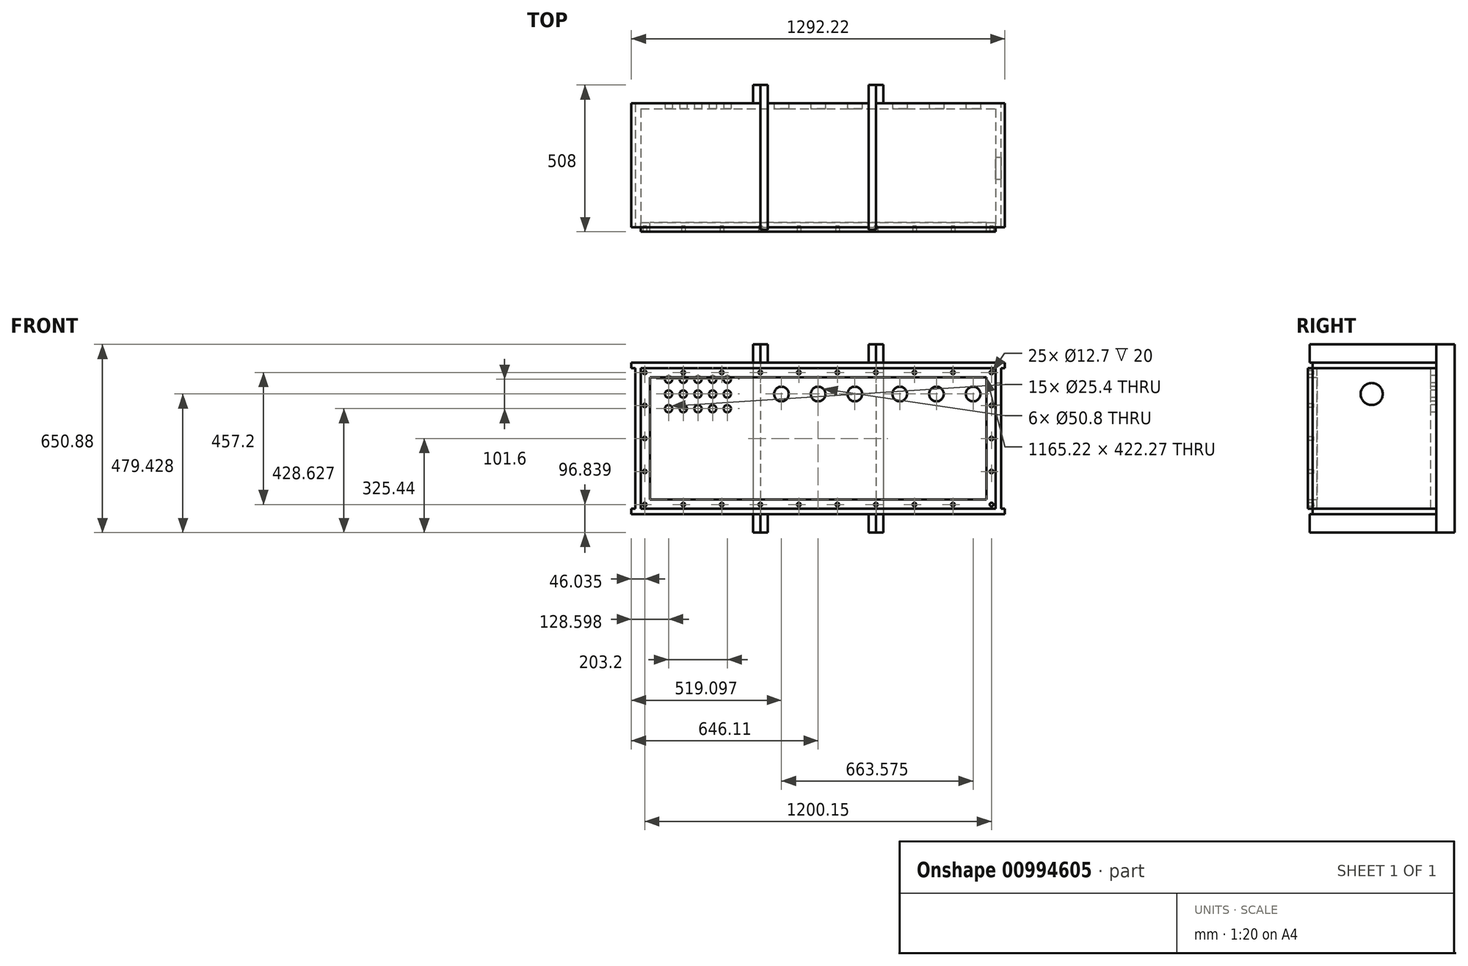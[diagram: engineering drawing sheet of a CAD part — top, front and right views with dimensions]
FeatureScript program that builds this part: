
annotation { "Feature Type Name" : "Feature", "Feature Type Description" : "" }
export const myFeature = defineFeature(function(context is Context, id is Id, definition is map)
    precondition{}
    {
        {
            var Q0;
            Q0=qCreatedBy(makeId("Front.planeOp"),FACE);
            var sketch = newSketch(context, id + "F0", { "sketchPlane" : qUnion([Q0])});
            skLineSegment(sketch, "E0.bottom", {"start": v(-633.41, -261.94) * mm, "end": v(633.41, -261.94) * mm});
            skLineSegment(sketch, "E0.top", {"start": v(-633.41, 261.94) * mm, "end": v(633.41, 261.94) * mm});
            skLineSegment(sketch, "E0.left", {"start": v(-633.41, -261.94) * mm, "end": v(-633.41, 261.94) * mm});
            skLineSegment(sketch, "E0.right", {"start": v(633.41, -261.94) * mm, "end": v(633.41, 261.94) * mm});
            skPoint(sketch, "E0.middle", {"position": v(0, 0) * mm});
            skSolve(sketch);
        }
        {
            var Q0;
            Q0=makeQuery(id+"F0.imprint","IMPRINT",FACE,{"disambiguationData":[TD([[makeQuery(id+"F0.imprint","IMPRINT",EDGE,{"derivedFrom":sQuery(id+"F0.wireOp",EDGE,"E0.bottom")}),1.0]])]});
            extrude(context, id + "F1", {"entities" : qUnion([Q0]), "depth" : 428.62 * mm, "offsetDistance" : 25 * mm});
        }
        {
            var Q0;
            Q0=makeQuery(id+"F1.opExtrude","CAP_FACE",FACE,{"disambiguationData":[OSD([sQuery(id+"F0.wireOp",EDGE,"E0.bottom"),sQuery(id+"F0.wireOp",EDGE,"E0.top"),sQuery(id+"F0.wireOp",EDGE,"E0.left"),sQuery(id+"F0.wireOp",EDGE,"E0.right")])],"isStart":false});
            var sketch = newSketch(context, id + "F2", { "sketchPlane" : qUnion([Q0])});
            skLineSegment(sketch, "E1.bottom", {"start": v(-614.36, -242.89) * mm, "end": v(614.36, -242.89) * mm});
            skLineSegment(sketch, "E1.top", {"start": v(-614.36, 242.89) * mm, "end": v(614.36, 242.89) * mm});
            skLineSegment(sketch, "E1.left", {"start": v(-614.36, -242.89) * mm, "end": v(-614.36, 242.89) * mm});
            skLineSegment(sketch, "E1.right", {"start": v(614.36, -242.89) * mm, "end": v(614.36, 242.89) * mm});
            skPoint(sketch, "E1.middle", {"position": v(0, 0) * mm});
            skSolve(sketch);
        }
        {
            var Q0;
            Q0=makeQuery(id+"F2.imprint","IMPRINT",FACE,{"disambiguationData":[TD([[makeQuery(id+"F2.imprint","IMPRINT",EDGE,{"derivedFrom":sQuery(id+"F2.wireOp",EDGE,"E1.bottom")}),1.0]])]});
            extrude(context, id + "F3", {"entities" : qUnion([Q0]), "operationType" : NewBodyOperationType.REMOVE, "oppositeDirection" : true, "depth" : 409.57 * mm, "offsetDistance" : 25 * mm});
        }
        {
            var Q0;
            Q0=makeQuery(id+"F1.opExtrude","CAP_FACE",FACE,{"disambiguationData":[OSD([sQuery(id+"F0.wireOp",EDGE,"E0.bottom"),sQuery(id+"F0.wireOp",EDGE,"E0.top"),sQuery(id+"F0.wireOp",EDGE,"E0.left"),sQuery(id+"F0.wireOp",EDGE,"E0.right")])],"isStart":false});
            var sketch = newSketch(context, id + "F4", { "sketchPlane" : qUnion([Q0])});
            skLineSegment(sketch, "E2.bottom", {"start": v(614.36, 242.89) * mm, "end": v(-614.36, 242.89) * mm});
            skLineSegment(sketch, "E2.top", {"start": v(614.36, -242.89) * mm, "end": v(-614.36, -242.89) * mm});
            skLineSegment(sketch, "E2.left", {"start": v(614.36, 242.89) * mm, "end": v(614.36, -242.89) * mm});
            skLineSegment(sketch, "E2.right", {"start": v(-614.36, 242.89) * mm, "end": v(-614.36, -242.89) * mm});
            skPoint(sketch, "E2.middle", {"position": v(0, 0) * mm});
            skLineSegment(sketch, "E3.bottom", {"start": v(582.61, 211.14) * mm, "end": v(-582.61, 211.14) * mm});
            skLineSegment(sketch, "E3.top", {"start": v(582.61, -211.14) * mm, "end": v(-582.61, -211.14) * mm});
            skLineSegment(sketch, "E3.left", {"start": v(582.61, 211.14) * mm, "end": v(582.61, -211.14) * mm});
            skLineSegment(sketch, "E3.right", {"start": v(-582.61, 211.14) * mm, "end": v(-582.61, -211.14) * mm});
            skSolve(sketch);
        }
        {
            var Q0;
            Q0 = qSketchRegion(id + "F4", true);
            extrude(context, id + "F5", {"entities" : qUnion([Q0]), "endBound" : BoundingType.SYMMETRIC, "depth" : 31.75 * mm, "offsetDistance" : 25 * mm});
        }
        {
            var Q0;
            Q0=makeQuery(id+"F5.opExtrude","CAP_FACE",FACE,{"disambiguationData":[OSD([sQuery(id+"F4.wireOp",EDGE,"E2.bottom"),sQuery(id+"F4.wireOp",EDGE,"E2.top"),sQuery(id+"F4.wireOp",EDGE,"E2.left"),sQuery(id+"F4.wireOp",EDGE,"E2.right"),sQuery(id+"F4.wireOp",EDGE,"E3.bottom"),sQuery(id+"F4.wireOp",EDGE,"E3.top"),sQuery(id+"F4.wireOp",EDGE,"E3.left"),sQuery(id+"F4.wireOp",EDGE,"E3.right")])],"isStart":false});
            var sketch = newSketch(context, id + "F6", { "sketchPlane" : qUnion([Q0])});
            skLineSegment(sketch, "E4", {"start": v(-600.08, 242.89) * mm, "end": v(-600.07, -242.89) * mm, "construction": true});
            skLineSegment(sketch, "E5", {"start": v(-614.36, 228.6) * mm, "end": v(614.36, 228.6) * mm, "construction": true});
            skLineSegment(sketch, "E6", {"start": v(-614.36, -228.6) * mm, "end": v(614.36, -228.6) * mm, "construction": true});
            skLineSegment(sketch, "E7", {"start": v(600.07, 242.89) * mm, "end": v(600.07, -242.89) * mm, "construction": true});
            skPoint(sketch, "E8", {"position": v(-600.08, 228.6) * mm});
            skCircle(sketch, "E9", {"center": v(-600.08, 228.6) * mm, "radius": 6.35 * mm});
            skCircle(sketch, "E10.1.0.0", {"center": v(-466.73, 228.6) * mm, "radius": 6.35 * mm});
            skCircle(sketch, "E10.2.0.0", {"center": v(-333.38, 228.6) * mm, "radius": 6.35 * mm});
            skCircle(sketch, "E10.3.0.0", {"center": v(-200.03, 228.6) * mm, "radius": 6.35 * mm});
            skCircle(sketch, "E10.4.0.0", {"center": v(-66.68, 228.6) * mm, "radius": 6.35 * mm});
            skCircle(sketch, "E10.5.0.0", {"center": v(66.67, 228.6) * mm, "radius": 6.35 * mm});
            skCircle(sketch, "E10.6.0.0", {"center": v(200.02, 228.6) * mm, "radius": 6.35 * mm});
            skCircle(sketch, "E10.7.0.0", {"center": v(333.37, 228.6) * mm, "radius": 6.35 * mm});
            skCircle(sketch, "E10.8.0.0", {"center": v(466.72, 228.6) * mm, "radius": 6.35 * mm});
            skCircle(sketch, "E10.9.0.0", {"center": v(600.07, 228.6) * mm, "radius": 6.35 * mm});
            skLineSegment(sketch, "E10.direction1", {"start": v(-600.08, 228.6) * mm, "end": v(-466.73, 228.6) * mm, "construction": true});
            skCircle(sketch, "E11.0.1.0", {"center": v(-600.08, 114.3) * mm, "radius": 6.35 * mm});
            skCircle(sketch, "E11.0.2.0", {"center": v(-600.08, 0) * mm, "radius": 6.35 * mm});
            skCircle(sketch, "E11.0.3.0", {"center": v(-600.08, -114.3) * mm, "radius": 6.35 * mm});
            skCircle(sketch, "E11.0.4.0", {"center": v(-600.08, -228.6) * mm, "radius": 6.35 * mm});
            skLineSegment(sketch, "E11.direction1", {"start": v(-600.08, 228.6) * mm, "end": v(-590.78, 228.6) * mm, "construction": true});
            skLineSegment(sketch, "E11.direction2", {"start": v(-600.08, 228.6) * mm, "end": v(-600.08, 114.3) * mm, "construction": true});
            skCircle(sketch, "E12.1.0.0", {"center": v(-466.73, -228.6) * mm, "radius": 6.35 * mm});
            skCircle(sketch, "E12.2.0.0", {"center": v(-333.38, -228.6) * mm, "radius": 6.35 * mm});
            skCircle(sketch, "E12.3.0.0", {"center": v(-200.03, -228.6) * mm, "radius": 6.35 * mm});
            skCircle(sketch, "E12.4.0.0", {"center": v(-66.68, -228.6) * mm, "radius": 6.35 * mm});
            skCircle(sketch, "E12.5.0.0", {"center": v(66.67, -228.6) * mm, "radius": 6.35 * mm});
            skCircle(sketch, "E12.6.0.0", {"center": v(200.02, -228.6) * mm, "radius": 6.35 * mm});
            skCircle(sketch, "E12.7.0.0", {"center": v(333.37, -228.6) * mm, "radius": 6.35 * mm});
            skCircle(sketch, "E12.8.0.0", {"center": v(466.72, -228.6) * mm, "radius": 6.35 * mm});
            skCircle(sketch, "E12.9.0.0", {"center": v(600.07, -228.6) * mm, "radius": 6.35 * mm});
            skLineSegment(sketch, "E12.direction1", {"start": v(-600.08, -228.6) * mm, "end": v(-466.73, -228.6) * mm, "construction": true});
            skCircle(sketch, "E13.0.1.0", {"center": v(600.07, 114.29) * mm, "radius": 6.35 * mm});
            skCircle(sketch, "E13.0.2.0", {"center": v(600.07, -0.02) * mm, "radius": 6.35 * mm});
            skCircle(sketch, "E13.0.3.0", {"center": v(600.07, -114.33) * mm, "radius": 6.35 * mm});
            skCircle(sketch, "E13.0.4.0", {"center": v(600.07, -228.64) * mm, "radius": 6.35 * mm});
            skLineSegment(sketch, "E13.direction1", {"start": v(600.07, 228.6) * mm, "end": v(625.07, 228.6) * mm, "construction": true});
            skLineSegment(sketch, "E13.direction2", {"start": v(600.07, 228.6) * mm, "end": v(600.07, 114.29) * mm, "construction": true});
            skSolve(sketch);
        }
        {
            var Q0;
            Q0 = qSketchRegion(id + "F6", true);
            var Q1;
            Q1=sQuery(id+"F6.wireOp",EDGE,"E9");
            extrude(context, id + "F7", {"entities" : qUnion([Q0]), "operationType" : NewBodyOperationType.REMOVE, "surfaceEntities" : qUnion([Q1]), "oppositeDirection" : true, "depth" : 20 * mm, "offsetDistance" : 25 * mm});
        }
        {
            var Q0;
            Q0=makeQuery(id+"F1.opExtrude","SWEPT_FACE",FACE,{"disambiguationData":[OSD([sQuery(id+"F0.wireOp",EDGE,"E0.left")])]});
            var sketch = newSketch(context, id + "F8", { "sketchPlane" : qUnion([Q0])});
            skLineSegment(sketch, "E14.bottom", {"start": v(0, -261.94) * mm, "end": v(428.63, -261.94) * mm});
            skLineSegment(sketch, "E14.top", {"start": v(0, -242.89) * mm, "end": v(428.63, -242.89) * mm});
            skLineSegment(sketch, "E14.left", {"start": v(0, -261.94) * mm, "end": v(0, -242.89) * mm});
            skLineSegment(sketch, "E14.right", {"start": v(428.63, -261.94) * mm, "end": v(428.63, -242.89) * mm});
            skLineSegment(sketch, "E15.bottom", {"start": v(0, 261.94) * mm, "end": v(428.63, 261.94) * mm});
            skLineSegment(sketch, "E15.top", {"start": v(0, 242.89) * mm, "end": v(428.63, 242.89) * mm});
            skLineSegment(sketch, "E15.left", {"start": v(0, 261.94) * mm, "end": v(0, 242.89) * mm});
            skLineSegment(sketch, "E15.right", {"start": v(428.63, 261.94) * mm, "end": v(428.63, 242.89) * mm});
            skLineSegment(sketch, "E16.bottom", {"start": v(0, 242.89) * mm, "end": v(19.05, 242.89) * mm});
            skLineSegment(sketch, "E16.top", {"start": v(0, -242.89) * mm, "end": v(19.05, -242.89) * mm});
            skLineSegment(sketch, "E16.left", {"start": v(0, 242.89) * mm, "end": v(0, -242.89) * mm});
            skLineSegment(sketch, "E16.right", {"start": v(19.05, 242.89) * mm, "end": v(19.05, -242.89) * mm});
            skSolve(sketch);
        }
        {
            var Q0;
            Q0=makeQuery(id+"F8.imprint","IMPRINT",FACE,{"disambiguationData":[TD([[makeQuery(id+"F8.imprint","IMPRINT",EDGE,{"derivedFrom":sQuery(id+"F8.wireOp",EDGE,"E14.bottom")}),-1.0]])]});
            var Q1;
            Q1=makeQuery(id+"F8.imprint","IMPRINT",FACE,{"disambiguationData":[TD([[makeQuery(id+"F8.imprint","IMPRINT",EDGE,{"derivedFrom":sQuery(id+"F8.wireOp",EDGE,"E15.bottom")}),1.0]])]});
            var Q2;
            Q2=makeQuery(id+"F8.imprint","IMPRINT",FACE,{"disambiguationData":[TD([[makeQuery(id+"F8.imprint","IMPRINT",EDGE,{"derivedFrom":sQuery(id+"F8.wireOp",EDGE,"E16.bottom")}),-1.0]])]});
            extrude(context, id + "F9", {"entities" : qUnion([Q0, Q1, Q2]), "operationType" : NewBodyOperationType.ADD, "depth" : 12.7 * mm, "offsetDistance" : 25 * mm});
        }
        {
            var Q0;
            Q0=makeQuery(id+"F1.opExtrude","SWEPT_FACE",FACE,{"disambiguationData":[OSD([sQuery(id+"F0.wireOp",EDGE,"E0.right")])]});
            var sketch = newSketch(context, id + "F10", { "sketchPlane" : qUnion([Q0])});
            skLineSegment(sketch, "E17.bottom", {"start": v(-428.63, 261.94) * mm, "end": v(0, 261.94) * mm});
            skLineSegment(sketch, "E17.top", {"start": v(-428.63, 242.89) * mm, "end": v(0, 242.89) * mm});
            skLineSegment(sketch, "E17.left", {"start": v(-428.63, 261.94) * mm, "end": v(-428.63, 242.89) * mm});
            skLineSegment(sketch, "E17.right", {"start": v(0, 261.94) * mm, "end": v(0, 242.89) * mm});
            skLineSegment(sketch, "E18.bottom", {"start": v(-428.63, -261.94) * mm, "end": v(0, -261.94) * mm});
            skLineSegment(sketch, "E18.top", {"start": v(-428.63, -242.89) * mm, "end": v(0, -242.89) * mm});
            skLineSegment(sketch, "E18.left", {"start": v(-428.63, -261.94) * mm, "end": v(-428.63, -242.89) * mm});
            skLineSegment(sketch, "E18.right", {"start": v(0, -261.94) * mm, "end": v(0, -242.89) * mm});
            skLineSegment(sketch, "E19.bottom", {"start": v(0, 242.89) * mm, "end": v(-19.05, 242.89) * mm});
            skLineSegment(sketch, "E19.top", {"start": v(0, -242.89) * mm, "end": v(-19.05, -242.89) * mm});
            skLineSegment(sketch, "E20.left", {"start": v(0, 242.89) * mm, "end": v(0, -242.89) * mm});
            skLineSegment(sketch, "E20.right", {"start": v(-19.05, 242.89) * mm, "end": v(-19.05, -242.89) * mm});
            skSolve(sketch);
        }
        {
            var Q0;
            Q0=makeQuery(id+"F10.imprint","IMPRINT",FACE,{"disambiguationData":[TD([[makeQuery(id+"F10.imprint","IMPRINT",EDGE,{"derivedFrom":sQuery(id+"F10.wireOp",EDGE,"E17.bottom")}),-1.0]])]});
            var Q1;
            Q1=makeQuery(id+"F10.imprint","IMPRINT",FACE,{"disambiguationData":[TD([[makeQuery(id+"F10.imprint","IMPRINT",EDGE,{"derivedFrom":sQuery(id+"F10.wireOp",EDGE,"E18.bottom")}),1.0]])]});
            var Q2;
            Q2=makeQuery(id+"F10.imprint","IMPRINT",FACE,{"disambiguationData":[TD([[makeQuery(id+"F10.imprint","IMPRINT",EDGE,{"derivedFrom":sQuery(id+"F10.wireOp",EDGE,"E19.bottom")}),1.0]])]});
            extrude(context, id + "F11", {"entities" : qUnion([Q0, Q1, Q2]), "operationType" : NewBodyOperationType.ADD, "depth" : 12.7 * mm, "offsetDistance" : 25 * mm});
        }
        {
            var Q0;
            Q0=qCreatedBy(makeId("Top.planeOp"),FACE);
            var sketch = newSketch(context, id + "F12", { "sketchPlane" : qUnion([Q0])});
            skLineSegment(sketch, "E21.bottom", {"start": v(225.43, 0) * mm, "end": v(200.03, 0) * mm});
            skLineSegment(sketch, "E21.top", {"start": v(225.43, 63.5) * mm, "end": v(200.03, 63.5) * mm});
            skLineSegment(sketch, "E21.left", {"start": v(225.43, 0) * mm, "end": v(225.43, 63.5) * mm});
            skLineSegment(sketch, "E21.right", {"start": v(200.03, 0) * mm, "end": v(200.03, 63.5) * mm});
            skLineSegment(sketch, "E22.bottom", {"start": v(-200.03, 0) * mm, "end": v(-225.43, 0) * mm});
            skLineSegment(sketch, "E22.top", {"start": v(-200.03, 63.5) * mm, "end": v(-225.43, 63.5) * mm});
            skLineSegment(sketch, "E22.left", {"start": v(-200.03, 0) * mm, "end": v(-200.03, 63.5) * mm});
            skLineSegment(sketch, "E22.right", {"start": v(-225.43, 0) * mm, "end": v(-225.43, 63.5) * mm});
            skSolve(sketch);
        }
        {
            var Q0;
            Q0=makeQuery(id+"F12.imprint","IMPRINT",FACE,{"disambiguationData":[TD([[makeQuery(id+"F12.imprint","IMPRINT",EDGE,{"derivedFrom":sQuery(id+"F12.wireOp",EDGE,"E22.bottom")}),-1.0]])]});
            var Q1;
            Q1=makeQuery(id+"F12.imprint","IMPRINT",FACE,{"disambiguationData":[TD([[makeQuery(id+"F12.imprint","IMPRINT",EDGE,{"derivedFrom":sQuery(id+"F12.wireOp",EDGE,"E21.bottom")}),-1.0]])]});
            extrude(context, id + "F13", {"entities" : qUnion([Q0, Q1]), "endBound" : BoundingType.SYMMETRIC, "depth" : 650.88 * mm, "offsetDistance" : 25 * mm});
        }
        {
            var Q0;
            Q0=makeQuery(id+"F13.opExtrude","SWEPT_FACE",FACE,{"disambiguationData":[OSD([sQuery(id+"F12.wireOp",EDGE,"E22.top")])]});
            var sketch = newSketch(context, id + "F14", { "sketchPlane" : qUnion([Q0])});
            skLineSegment(sketch, "E23.bottom", {"start": v(200.03, 325.44) * mm, "end": v(174.63, 325.44) * mm});
            skLineSegment(sketch, "E23.top", {"start": v(200.03, 261.94) * mm, "end": v(174.63, 261.94) * mm});
            skLineSegment(sketch, "E23.left", {"start": v(200.03, 325.44) * mm, "end": v(200.03, 261.94) * mm});
            skLineSegment(sketch, "E23.right", {"start": v(174.63, 325.44) * mm, "end": v(174.63, 261.94) * mm});
            skLineSegment(sketch, "E24.bottom", {"start": v(-200.03, 325.44) * mm, "end": v(-174.62, 325.44) * mm});
            skLineSegment(sketch, "E24.top", {"start": v(-200.03, 261.94) * mm, "end": v(-174.62, 261.94) * mm});
            skLineSegment(sketch, "E24.left", {"start": v(-200.03, 325.44) * mm, "end": v(-200.03, 261.94) * mm});
            skLineSegment(sketch, "E24.right", {"start": v(-174.62, 325.44) * mm, "end": v(-174.62, 261.94) * mm});
            skSolve(sketch);
        }
        {
            var Q0;
            Q0=makeQuery(id+"F14.imprint","IMPRINT",FACE,{"disambiguationData":[TD([[makeQuery(id+"F14.imprint","IMPRINT",EDGE,{"derivedFrom":sQuery(id+"F14.wireOp",EDGE,"E23.bottom")}),1.0]])]});
            var Q1;
            Q1=makeQuery(id+"F14.imprint","IMPRINT",FACE,{"disambiguationData":[TD([[makeQuery(id+"F14.imprint","IMPRINT",EDGE,{"derivedFrom":sQuery(id+"F14.wireOp",EDGE,"E24.bottom")}),-1.0]])]});
            extrude(context, id + "F15", {"entities" : qUnion([Q0, Q1]), "oppositeDirection" : true, "depth" : 501.65 * mm, "offsetDistance" : 25 * mm});
        }
        {
            var Q0;
            Q0=makeQuery(id+"F13.opExtrude","SWEPT_FACE",FACE,{"disambiguationData":[OSD([sQuery(id+"F12.wireOp",EDGE,"E21.top")])]});
            var sketch = newSketch(context, id + "F16", { "sketchPlane" : qUnion([Q0])});
            skLineSegment(sketch, "E25.bottom", {"start": v(200.03, -325.44) * mm, "end": v(174.63, -325.44) * mm});
            skLineSegment(sketch, "E25.top", {"start": v(200.03, -261.94) * mm, "end": v(174.63, -261.94) * mm});
            skLineSegment(sketch, "E25.left", {"start": v(200.03, -325.44) * mm, "end": v(200.03, -261.94) * mm});
            skLineSegment(sketch, "E25.right", {"start": v(174.63, -325.44) * mm, "end": v(174.63, -261.94) * mm});
            skLineSegment(sketch, "E26.bottom", {"start": v(-200.03, -325.44) * mm, "end": v(-174.62, -325.44) * mm});
            skLineSegment(sketch, "E26.top", {"start": v(-200.03, -261.94) * mm, "end": v(-174.62, -261.94) * mm});
            skLineSegment(sketch, "E26.left", {"start": v(-200.03, -325.44) * mm, "end": v(-200.03, -261.94) * mm});
            skLineSegment(sketch, "E26.right", {"start": v(-174.62, -325.44) * mm, "end": v(-174.62, -261.94) * mm});
            skSolve(sketch);
        }
        {
            var Q0;
            Q0=makeQuery(id+"F16.imprint","IMPRINT",FACE,{"disambiguationData":[TD([[makeQuery(id+"F16.imprint","IMPRINT",EDGE,{"derivedFrom":sQuery(id+"F16.wireOp",EDGE,"E26.bottom")}),1.0]])]});
            var Q1;
            Q1=makeQuery(id+"F16.imprint","IMPRINT",FACE,{"disambiguationData":[TD([[makeQuery(id+"F16.imprint","IMPRINT",EDGE,{"derivedFrom":sQuery(id+"F16.wireOp",EDGE,"E25.bottom")}),-1.0]])]});
            extrude(context, id + "F17", {"entities" : qUnion([Q0, Q1]), "oppositeDirection" : true, "depth" : 501.65 * mm, "offsetDistance" : 25 * mm});
        }
        {
            var Q0;
            Q0=makeQuery(id+"F3.boolean.opBoolean","COPY",FACE,{"derivedFrom":makeQuery(id+"F3.opExtrude","CAP_FACE",FACE,{"disambiguationData":[OSD([sQuery(id+"F2.wireOp",EDGE,"E1.bottom"),sQuery(id+"F2.wireOp",EDGE,"E1.top"),sQuery(id+"F2.wireOp",EDGE,"E1.left"),sQuery(id+"F2.wireOp",EDGE,"E1.right")])],"isStart":false})});
            var sketch = newSketch(context, id + "F18", { "sketchPlane" : qUnion([Q0])});
            skSolve(sketch);
        }
        {
            var Q0;
            Q0=makeQuery(id+"F11.boolean.opBoolean","MERGE",FACE,{"derivedFrom":[makeQuery(id+"F9.boolean.opBoolean","MERGE",FACE,{"derivedFrom":[makeQuery(id+"F1.opExtrude","SWEPT_FACE",FACE,{"disambiguationData":[OSD([sQuery(id+"F0.wireOp",EDGE,"E0.top")])]}),makeQuery(id+"F9.opExtrude","SWEPT_FACE",FACE,{"disambiguationData":[OSD([sQuery(id+"F8.wireOp",EDGE,"E15.bottom")])]})]}),makeQuery(id+"F11.opExtrude","SWEPT_FACE",FACE,{"disambiguationData":[OSD([sQuery(id+"F10.wireOp",EDGE,"E17.bottom")])]})]});
            var sketch = newSketch(context, id + "F19", { "sketchPlane" : qUnion([Q0])});
            skLineSegment(sketch, "E27.0", {"start": v(-646.11, 0) * mm, "end": v(646.11, 0) * mm});
            skLineSegment(sketch, "E28.0", {"start": v(-200.02, -438.15) * mm, "end": v(-200.03, 63.5) * mm});
            skPoint(sketch, "E29", {"position": v(-200.03, 0) * mm});
            skLineSegment(sketch, "E30", {"start": v(-200.03, 0) * mm, "end": v(-207.13, -92.38) * mm, "construction": true});
            skSolve(sketch);
        }
        {
            var Q0;
            Q0=makeQuery(id+"F18.imprint","IMPRINT",FACE,{"disambiguationData":[TD([[makeQuery(id+"F18.imprint","IMPRINT",EDGE,{"derivedFrom":makeQuery(id+"F3.boolean.opBoolean","COPY",EDGE,{"derivedFrom":makeQuery(id+"F3.opExtrude","CAP_EDGE",EDGE,{"disambiguationData":[OSD([sQuery(id+"F2.wireOp",EDGE,"E1.bottom")])],"isStart":false})})}),1.0]])]});
            var sketch = newSketch(context, id + "F20", { "sketchPlane" : qUnion([Q0])});
            skLineSegment(sketch, "E31.0", {"start": v(-614.36, 242.89) * mm, "end": v(614.36, 242.89) * mm});
            skLineSegment(sketch, "E32.0", {"start": v(-614.36, -242.89) * mm, "end": v(-614.36, 242.89) * mm});
            skLineSegment(sketch, "E33", {"start": v(126.99, 242.89) * mm, "end": v(126.99, 153.99) * mm, "construction": true});
            skCircle(sketch, "E34", {"center": v(126.99, 153.99) * mm, "radius": 25.4 * mm});
            skCircle(sketch, "E35.2.0.0", {"center": v(282.56, 153.99) * mm, "radius": 25.4 * mm});
            skCircle(sketch, "E35.3.0.0", {"center": v(409.56, 153.99) * mm, "radius": 25.4 * mm});
            skCircle(sketch, "E35.4.0.0", {"center": v(536.56, 153.99) * mm, "radius": 25.4 * mm});
            skLineSegment(sketch, "E36", {"start": v(-614.36, 204.79) * mm, "end": v(-517.51, 204.79) * mm, "construction": true});
            skLineSegment(sketch, "E37", {"start": v(-0.01, 242.89) * mm, "end": v(-0.01, 153.99) * mm, "construction": true});
            skCircle(sketch, "E38", {"center": v(-0.01, 153.99) * mm, "radius": 25.4 * mm});
            skCircle(sketch, "E39", {"center": v(-517.51, 204.79) * mm, "radius": 12.7 * mm});
            skCircle(sketch, "E40.0.1.0", {"center": v(-517.51, 153.99) * mm, "radius": 12.7 * mm});
            skCircle(sketch, "E40.0.2.0", {"center": v(-517.51, 103.19) * mm, "radius": 12.7 * mm});
            skCircle(sketch, "E40.1.0.0", {"center": v(-466.71, 204.79) * mm, "radius": 12.7 * mm});
            skCircle(sketch, "E40.1.1.0", {"center": v(-466.71, 153.99) * mm, "radius": 12.7 * mm});
            skCircle(sketch, "E40.1.2.0", {"center": v(-466.71, 103.19) * mm, "radius": 12.7 * mm});
            skCircle(sketch, "E40.2.0.0", {"center": v(-415.91, 204.79) * mm, "radius": 12.7 * mm});
            skCircle(sketch, "E40.2.1.0", {"center": v(-415.91, 153.99) * mm, "radius": 12.7 * mm});
            skCircle(sketch, "E40.2.2.0", {"center": v(-415.91, 103.19) * mm, "radius": 12.7 * mm});
            skCircle(sketch, "E40.3.0.0", {"center": v(-365.11, 204.79) * mm, "radius": 12.7 * mm});
            skCircle(sketch, "E40.3.1.0", {"center": v(-365.11, 153.99) * mm, "radius": 12.7 * mm});
            skCircle(sketch, "E40.3.2.0", {"center": v(-365.11, 103.19) * mm, "radius": 12.7 * mm});
            skCircle(sketch, "E40.4.0.0", {"center": v(-314.31, 204.79) * mm, "radius": 12.7 * mm});
            skCircle(sketch, "E40.4.1.0", {"center": v(-314.31, 153.99) * mm, "radius": 12.7 * mm});
            skCircle(sketch, "E40.4.2.0", {"center": v(-314.31, 103.19) * mm, "radius": 12.7 * mm});
            skLineSegment(sketch, "E40.direction1", {"start": v(-517.51, 204.79) * mm, "end": v(-466.71, 204.79) * mm, "construction": true});
            skLineSegment(sketch, "E40.direction2", {"start": v(-517.51, 204.79) * mm, "end": v(-517.51, 153.99) * mm, "construction": true});
            skLineSegment(sketch, "E41", {"start": v(-127.01, 242.89) * mm, "end": v(-127.01, 153.99) * mm, "construction": true});
            skCircle(sketch, "E42", {"center": v(-127.01, 153.99) * mm, "radius": 25.4 * mm});
            skPoint(sketch, "E43", {"position": v(-200.03, 242.89) * mm});
            skPoint(sketch, "E44.0", {"position": v(-200.03, 261.94) * mm});
            skLineSegment(sketch, "E45", {"start": v(536.56, 153.99) * mm, "end": v(-145.46, 153.99) * mm, "construction": true});
            skSolve(sketch);
        }
        {
            var Q0;
            Q0=makeQuery(id+"F20.imprint","IMPRINT",FACE,{"disambiguationData":[TD([[makeQuery(id+"F20.imprint","IMPRINT",EDGE,{"derivedFrom":sQuery(id+"F20.wireOp",EDGE,"E38")}),1.0]])]});
            var Q1;
            Q1=makeQuery(id+"F20.imprint","IMPRINT",FACE,{"disambiguationData":[TD([[makeQuery(id+"F20.imprint","IMPRINT",EDGE,{"derivedFrom":sQuery(id+"F20.wireOp",EDGE,"E35.4.0.0")}),1.0]])]});
            var Q2;
            Q2=makeQuery(id+"F20.imprint","IMPRINT",FACE,{"disambiguationData":[TD([[makeQuery(id+"F20.imprint","IMPRINT",EDGE,{"derivedFrom":sQuery(id+"F20.wireOp",EDGE,"E35.3.0.0")}),1.0]])]});
            var Q3;
            Q3=makeQuery(id+"F20.imprint","IMPRINT",FACE,{"disambiguationData":[TD([[makeQuery(id+"F20.imprint","IMPRINT",EDGE,{"derivedFrom":sQuery(id+"F20.wireOp",EDGE,"E35.2.0.0")}),1.0]])]});
            var Q4;
            Q4=makeQuery(id+"F20.imprint","IMPRINT",FACE,{"disambiguationData":[TD([[makeQuery(id+"F20.imprint","IMPRINT",EDGE,{"derivedFrom":sQuery(id+"F20.wireOp",EDGE,"E34")}),1.0]])]});
            extrude(context, id + "F21", {"entities" : qUnion([Q0, Q1, Q2, Q3, Q4]), "operationType" : NewBodyOperationType.REMOVE, "oppositeDirection" : true, "depth" : 25 * mm, "offsetDistance" : 25 * mm});
        }
        {
            var Q0;
            Q0 = qSketchRegion(id + "F20", true);
            extrude(context, id + "F22", {"entities" : qUnion([Q0]), "operationType" : NewBodyOperationType.REMOVE, "oppositeDirection" : true, "depth" : 25 * mm, "offsetDistance" : 25 * mm});
        }
        {
            var Q0;
            Q0=makeQuery(id+"F1.opExtrude","SWEPT_FACE",FACE,{"disambiguationData":[OSD([sQuery(id+"F0.wireOp",EDGE,"E0.right")])]});
            var sketch = newSketch(context, id + "F23", { "sketchPlane" : qUnion([Q0])});
            skCircle(sketch, "E46", {"center": v(-223.85, 153.99) * mm, "radius": 38.1 * mm});
            skLineSegment(sketch, "E47.0", {"start": v(-19.05, 242.89) * mm, "end": v(-19.05, -242.89) * mm});
            skSolve(sketch);
        }
        {
            var Q0;
            Q0=makeQuery(id+"F23.imprint","IMPRINT",FACE,{"disambiguationData":[TD([[makeQuery(id+"F23.imprint","IMPRINT",EDGE,{"derivedFrom":sQuery(id+"F23.wireOp",EDGE,"E46")}),1.0]])]});
            extrude(context, id + "F24", {"entities" : qUnion([Q0]), "operationType" : NewBodyOperationType.REMOVE, "oppositeDirection" : true, "depth" : 25 * mm, "offsetDistance" : 25 * mm});
        }
    });
